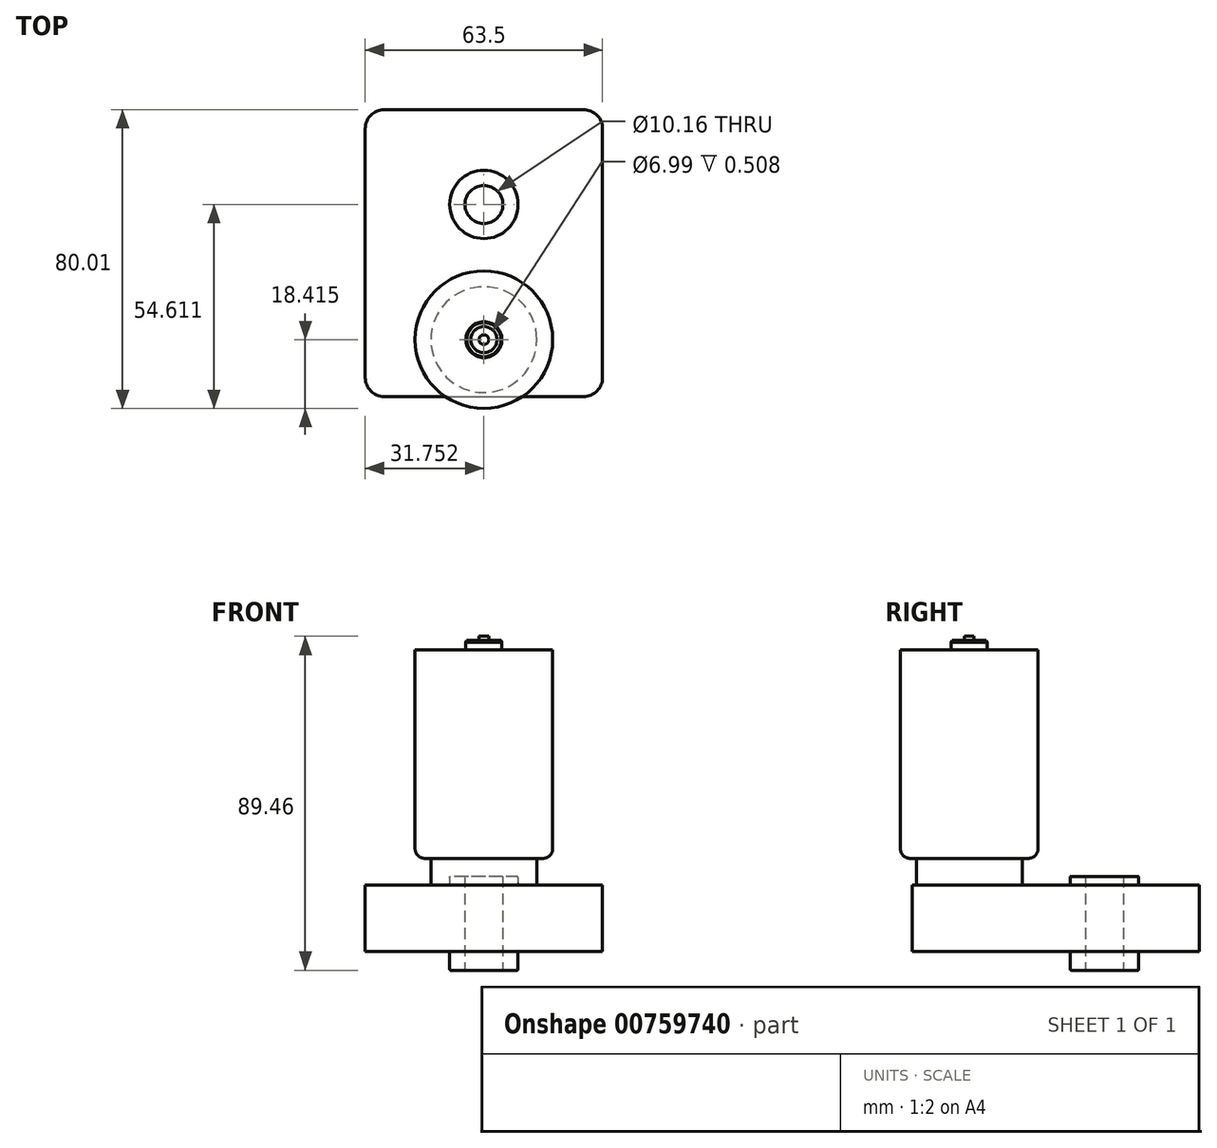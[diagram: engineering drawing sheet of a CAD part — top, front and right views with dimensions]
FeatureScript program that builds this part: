
annotation { "Feature Type Name" : "Feature", "Feature Type Description" : "" }
export const myFeature = defineFeature(function(context is Context, id is Id, definition is map)
    precondition{}
    {
        {
            var Q0;
            Q0=qCreatedBy(makeId("Top.planeOp"),FACE);
            var sketch = newSketch(context, id + "F0", { "sketchPlane" : qUnion([Q0])});
            skLineSegment(sketch, "E0.bottom", {"start": v(-41.88, -41.7) * mm, "end": v(21.62, -41.7) * mm});
            skLineSegment(sketch, "E0.top", {"start": v(-41.88, 35.14) * mm, "end": v(21.62, 35.14) * mm});
            skLineSegment(sketch, "E0.left", {"start": v(-41.88, -41.7) * mm, "end": v(-41.88, 35.14) * mm});
            skLineSegment(sketch, "E0.right", {"start": v(21.62, -41.7) * mm, "end": v(21.62, 35.14) * mm});
            skLineSegment(sketch, "E1", {"start": v(-10.13, 35.14) * mm, "end": v(-10.13, 9.74) * mm, "construction": true});
            skCircle(sketch, "E2", {"center": v(-10.13, 9.74) * mm, "radius": 9.14 * mm});
            skCircle(sketch, "E3", {"center": v(-10.13, 9.74) * mm, "radius": 5.08 * mm});
            skCircle(sketch, "E4", {"center": v(-10.13, 9.74) * mm, "radius": 4.45 * mm});
            skLineSegment(sketch, "E5", {"start": v(-10.13, -41.7) * mm, "end": v(-10.13, -26.45) * mm, "construction": true});
            skCircle(sketch, "E6", {"center": v(-10.13, -26.45) * mm, "radius": 14.17 * mm});
            skLineSegment(sketch, "E7", {"start": v(21.62, -3.28) * mm, "end": v(-10.13, -3.28) * mm, "construction": true});
            skSolve(sketch);
        }
        {
            var Q0;
            Q0=makeQuery(id+"F0.imprint","IMPRINT",FACE,{"disambiguationData":[TD([[makeQuery(id+"F0.imprint","IMPRINT",EDGE,{"derivedFrom":sQuery(id+"F0.wireOp",EDGE,"E0.bottom")}),1.0]])]});
            var Q1;
            Q1=makeQuery(id+"F0.imprint","IMPRINT",FACE,{"disambiguationData":[TD([[makeQuery(id+"F0.imprint","IMPRINT",EDGE,{"derivedFrom":sQuery(id+"F0.wireOp",EDGE,"E4")}),1.0]])]});
            var Q2;
            Q2=makeQuery(id+"F0.imprint","IMPRINT",FACE,{"disambiguationData":[TD([[makeQuery(id+"F0.imprint","IMPRINT",EDGE,{"derivedFrom":sQuery(id+"F0.wireOp",EDGE,"E6")}),1.0]])]});
            var Q3;
            Q3=makeQuery(id+"F0.imprint","IMPRINT",FACE,{"disambiguationData":[TD([[makeQuery(id+"F0.imprint","IMPRINT",EDGE,{"derivedFrom":sQuery(id+"F0.wireOp",EDGE,"E2")}),1.0]])]});
            var Q4;
            Q4=makeQuery(id+"F0.imprint","IMPRINT",FACE,{"disambiguationData":[TD([[makeQuery(id+"F0.imprint","IMPRINT",EDGE,{"derivedFrom":sQuery(id+"F0.wireOp",EDGE,"E3")}),1.0]])]});
            extrude(context, id + "F1", {"entities" : qUnion([Q0, Q1, Q2, Q3, Q4]), "depth" : 17.78 * mm, "offsetDistance" : 25.4 * mm});
        }
        {
            var Q0;
            Q0=makeQuery(id+"F0.imprint","IMPRINT",FACE,{"disambiguationData":[TD([[makeQuery(id+"F0.imprint","IMPRINT",EDGE,{"derivedFrom":sQuery(id+"F0.wireOp",EDGE,"E6")}),1.0]])]});
            extrude(context, id + "F2", {"entities" : qUnion([Q0]), "operationType" : NewBodyOperationType.ADD, "depth" : 24.9 * mm, "offsetDistance" : 25.4 * mm});
        }
        {
            var Q0;
            Q0=makeQuery(id+"F0.imprint","IMPRINT",FACE,{"disambiguationData":[TD([[makeQuery(id+"F0.imprint","IMPRINT",EDGE,{"derivedFrom":sQuery(id+"F0.wireOp",EDGE,"E2")}),1.0]])]});
            extrude(context, id + "F3", {"entities" : qUnion([Q0]), "operationType" : NewBodyOperationType.ADD, "depth" : 20.07 * mm, "offsetDistance" : 25.4 * mm});
        }
        {
            var Q0;
            Q0=makeQuery(id+"F3.boolean.opBoolean","SPLIT",FACE,{"disambiguationData":[TD([makeQuery(id+"F3.opExtrude","SWEPT_FACE",FACE,{"disambiguationData":[OSD([sQuery(id+"F0.wireOp",EDGE,"E3")])]})])],"derivedFrom":makeQuery(id+"F1.opExtrude","CAP_FACE",FACE,{"disambiguationData":[OSD([sQuery(id+"F0.wireOp",EDGE,"E0.bottom"),sQuery(id+"F0.wireOp",EDGE,"E0.top"),sQuery(id+"F0.wireOp",EDGE,"E0.left"),sQuery(id+"F0.wireOp",EDGE,"E0.right")])],"isStart":false})});
            extrude(context, id + "F4", {"entities" : qUnion([Q0]), "operationType" : NewBodyOperationType.REMOVE, "oppositeDirection" : true, "depth" : 25.4 * mm, "offsetDistance" : 25.4 * mm});
        }
        {
            var Q0;
            Q0=makeQuery(id+"F2.opExtrude","CAP_FACE",FACE,{"disambiguationData":[OSD([sQuery(id+"F0.wireOp",EDGE,"E6")])],"isStart":false});
            var sketch = newSketch(context, id + "F5", { "sketchPlane" : qUnion([Q0])});
            skCircle(sketch, "E8", {"center": v(-10.13, -26.45) * mm, "radius": 18.41 * mm});
            skSolve(sketch);
        }
        {
            var Q0;
            Q0=makeQuery(id+"F5.imprint","IMPRINT",FACE,{"disambiguationData":[TD([[makeQuery(id+"F5.imprint","IMPRINT",EDGE,{"derivedFrom":sQuery(id+"F5.wireOp",EDGE,"E8")}),1.0]])]});
            var Q1;
            Q1=makeQuery(id+"F5.imprint","IMPRINT",FACE,{"disambiguationData":[TD([[makeQuery(id+"F5.imprint","IMPRINT",EDGE,{"derivedFrom":makeQuery(id+"F2.opExtrude","CAP_EDGE",EDGE,{"disambiguationData":[OSD([sQuery(id+"F0.wireOp",EDGE,"E6")])],"isStart":false})}),1.0]])]});
            extrude(context, id + "F6", {"entities" : qUnion([Q0, Q1]), "operationType" : NewBodyOperationType.ADD, "depth" : 55.88 * mm, "offsetDistance" : 25.4 * mm});
        }
        {
            var Q0;
            Q0=makeQuery(id+"F0.imprint","IMPRINT",FACE,{"disambiguationData":[TD([[makeQuery(id+"F0.imprint","IMPRINT",EDGE,{"derivedFrom":sQuery(id+"F0.wireOp",EDGE,"E2")}),1.0]])]});
            extrude(context, id + "F7", {"entities" : qUnion([Q0]), "operationType" : NewBodyOperationType.ADD, "oppositeDirection" : true, "depth" : 5.08 * mm, "offsetDistance" : 25.4 * mm});
        }
        {
            var Q0;
            Q0=makeQuery(id+"F1.opExtrude","SWEPT_EDGE",EDGE,{"disambiguationData":[OSD([sQuery(id+"F0.wireOp",EDGE,"E0.top"),sQuery(id+"F0.wireOp",EDGE,"E0.left")])]});
            var Q1;
            Q1=makeQuery(id+"F1.opExtrude","SWEPT_EDGE",EDGE,{"disambiguationData":[OSD([sQuery(id+"F0.wireOp",EDGE,"E0.top"),sQuery(id+"F0.wireOp",EDGE,"E0.right")])]});
            var Q2;
            Q2=makeQuery(id+"F1.opExtrude","SWEPT_EDGE",EDGE,{"disambiguationData":[OSD([sQuery(id+"F0.wireOp",EDGE,"E0.bottom"),sQuery(id+"F0.wireOp",EDGE,"E0.right")])]});
            var Q3;
            Q3=makeQuery(id+"F1.opExtrude","SWEPT_EDGE",EDGE,{"disambiguationData":[OSD([sQuery(id+"F0.wireOp",EDGE,"E0.bottom"),sQuery(id+"F0.wireOp",EDGE,"E0.left")])]});
            fillet(context, id + "F8", {"entities" : qUnion([Q0, Q1, Q2, Q3]), "radius" : 5.08 * mm, "tangentPropagation" : true, "allowEdgeOverflow" : false});
        }
        {
            var Q0;
            Q0=makeQuery(id+"F3.boolean.opBoolean","INTERSECT",EDGE,{"derivedFrom":[makeQuery(id+"F1.opExtrude","CAP_FACE",FACE,{"disambiguationData":[OSD([sQuery(id+"F0.wireOp",EDGE,"E0.bottom"),sQuery(id+"F0.wireOp",EDGE,"E0.top"),sQuery(id+"F0.wireOp",EDGE,"E0.left"),sQuery(id+"F0.wireOp",EDGE,"E0.right")])],"isStart":false}),makeQuery(id+"F3.opExtrude","SWEPT_FACE",FACE,{"disambiguationData":[OSD([sQuery(id+"F0.wireOp",EDGE,"E2")])]})]});
            var Q1;
            Q1=makeQuery(id+"F3.opExtrude","SWEPT_FACE",FACE,{"disambiguationData":[OSD([sQuery(id+"F0.wireOp",EDGE,"E2")])]});
            var Q2;
            Q2=makeQuery(id+"F7.opExtrude","CAP_EDGE",EDGE,{"disambiguationData":[OSD([sQuery(id+"F0.wireOp",EDGE,"E2")])],"isStart":true});
            var Q3;
            Q3=makeQuery(id+"F7.opExtrude","CAP_EDGE",EDGE,{"disambiguationData":[OSD([sQuery(id+"F0.wireOp",EDGE,"E2")])],"isStart":false});
            fillet(context, id + "F9", {"entities" : qUnion([Q0, Q1, Q2, Q3]), "radius" : 0.25 * mm, "tangentPropagation" : true, "allowEdgeOverflow" : false});
        }
        {
            var Q0;
            Q0=makeQuery(id+"F6.opExtrude","CAP_EDGE",EDGE,{"disambiguationData":[OSD([sQuery(id+"F5.wireOp",EDGE,"E8")])],"isStart":true});
            fillet(context, id + "F10", {"entities" : qUnion([Q0]), "radius" : 2.54 * mm, "tangentPropagation" : true, "allowEdgeOverflow" : false});
        }
        {
            var Q0;
            Q0=makeQuery(id+"F2.boolean.opBoolean","INTERSECT",EDGE,{"derivedFrom":[makeQuery(id+"F1.opExtrude","CAP_FACE",FACE,{"disambiguationData":[OSD([sQuery(id+"F0.wireOp",EDGE,"E0.bottom"),sQuery(id+"F0.wireOp",EDGE,"E0.top"),sQuery(id+"F0.wireOp",EDGE,"E0.left"),sQuery(id+"F0.wireOp",EDGE,"E0.right")])],"isStart":false}),makeQuery(id+"F2.opExtrude","SWEPT_FACE",FACE,{"disambiguationData":[OSD([sQuery(id+"F0.wireOp",EDGE,"E6")])]})]});
            fillet(context, id + "F11", {"entities" : qUnion([Q0]), "radius" : 0.25 * mm, "tangentPropagation" : true, "allowEdgeOverflow" : false});
        }
        {
            var Q0;
            Q0=makeQuery(id+"F6.opExtrude","CAP_FACE",FACE,{"disambiguationData":[OSD([sQuery(id+"F5.wireOp",EDGE,"E8")])],"isStart":false});
            var sketch = newSketch(context, id + "F12", { "sketchPlane" : qUnion([Q0])});
            skCircle(sketch, "E9", {"center": v(-10.13, -26.45) * mm, "radius": 4.83 * mm});
            skCircle(sketch, "E10", {"center": v(-10.13, -26.45) * mm, "radius": 3.5 * mm});
            skCircle(sketch, "E11", {"center": v(-10.13, -26.45) * mm, "radius": 1.3 * mm});
            skSolve(sketch);
        }
        {
            var Q0;
            Q0=makeQuery(id+"F12.imprint","IMPRINT",FACE,{"disambiguationData":[TD([[makeQuery(id+"F12.imprint","IMPRINT",EDGE,{"derivedFrom":sQuery(id+"F12.wireOp",EDGE,"E9")}),1.0]])]});
            extrude(context, id + "F13", {"entities" : qUnion([Q0]), "operationType" : NewBodyOperationType.ADD, "depth" : 2.54 * mm, "offsetDistance" : 25.4 * mm});
        }
        {
            var Q0;
            Q0=makeQuery(id+"F12.imprint","IMPRINT",FACE,{"disambiguationData":[TD([[makeQuery(id+"F12.imprint","IMPRINT",EDGE,{"derivedFrom":sQuery(id+"F12.wireOp",EDGE,"E11")}),1.0]])]});
            extrude(context, id + "F14", {"entities" : qUnion([Q0]), "operationType" : NewBodyOperationType.ADD, "depth" : 3.6 * mm, "offsetDistance" : 25.4 * mm});
        }
        {
            var Q0;
            Q0=makeQuery(id+"F12.imprint","IMPRINT",FACE,{"disambiguationData":[TD([[makeQuery(id+"F12.imprint","IMPRINT",EDGE,{"derivedFrom":sQuery(id+"F12.wireOp",EDGE,"E10")}),1.0]])]});
            extrude(context, id + "F15", {"entities" : qUnion([Q0]), "operationType" : NewBodyOperationType.ADD, "depth" : 2.03 * mm, "offsetDistance" : 25.4 * mm});
        }
        {
            var Q0;
            Q0=makeQuery(id+"F13.opExtrude","CAP_EDGE",EDGE,{"disambiguationData":[OSD([sQuery(id+"F12.wireOp",EDGE,"E9")])],"isStart":false});
            chamfer(context, id + "F16", {"entities" : qUnion([Q0]), "chamferType" : ChamferType.TWO_OFFSETS, "width1" : 0.25 * mm, "oppositeDirection" : false, "width2" : 0.5 * mm, "tangentPropagation" : true});
        }
    });
